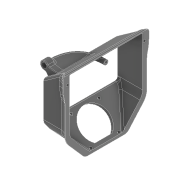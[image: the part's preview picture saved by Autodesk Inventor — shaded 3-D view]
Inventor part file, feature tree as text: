
AUTODESK INVENTOR PART (.ipt)
format: ipt  version: 2021 (Build 250183000, 183)  size: 3,283,456 bytes
history: native  units: mm
features: sketch x21, extrude x16, fillet x15, projected_geometry x11, reference x6, chamfer x5, plane x4, sweep x4, delete_face x3, other x3, hole x1, thread x1
ambient origin geometry x8: Origin, YZ Plane, XZ Plane, XY Plane, X Axis, Y Axis, Z Axis, Center Point
bodies: Volumenkörper1 (feature_tree), Body6 (feature_tree)
feature tree (90):
  extrude  "Extrusion1"  Depth=3.0mm TaperAngle=0.0deg
  extrude  "Extrusion2"  Depth=11.5mm
  fillet  "Rundung1"  Radius=4.6mm
  fillet  "Rundung3"  Radius=4.6mm
  extrude  "Extrusion3"  Depth=10.0mm
  sketch  "Skizze5"  dims[d13=1.0mm d14=4.1mm]
  plane  "Arbeitsebene1"
  sketch  "Skizze6"  dims[d15=8.1mm d16=0.0mm d17=0.0mm]
  sweep  "Sweeping1"
  extrude  "Extrusion4"  TaperAngle=0.0deg  [1 undecoded]
  sketch  "Skizze9"  dims[d28=9.7mm d29=19.456mm d30=4.0mm d31=2.0mm d32=90.0deg d33=11.0mm d34=0.0mm d35=14.0mm d36=0.0mm]
  sketch  "Skizze10"  dims[d37=14.0mm d38=0.0mm d39=45.0mm d40=0.0mm]
  hole  "Bohrung1"  [1 undecoded]
  extrude  "Extrusion5"  Depth=14.0mm TaperAngle=0.0deg
  extrude  "Extrusion6"  Depth=45.0mm TaperAngle=0.0deg
  extrude  "Extrusion7"  Depth=10.0mm TaperAngle=0.0deg
  extrude  "Extrusion8"  Depth=10.0mm TaperAngle=0.0deg
  plane  "Arbeitsebene3"
  extrude  "Extrusion9"  Depth=30.0mm TaperAngle=0.0deg
  plane  "Arbeitsebene2"
  extrude  "Extrusion10"  TaperAngle=0.0deg  [1 undecoded]
  sweep  "Sweeping2"
  extrude  "Extrusion11"  Depth=10.0mm TaperAngle=0.0deg
  extrude  "Extrusion12"  Depth=5.0mm
  sweep  "Sweeping3"
  extrude  "Extrusion13"  Depth=4.0mm
  fillet  "Rundung8"  Radius=9.599311mm
  fillet  "Rundung9"  Radius=9.599311mm
  extrude  "Extrusion14"  TaperAngle=0.0deg  [1 undecoded]
  fillet  "Rundung10"  Radius=10.0mm
  fillet  "Rundung11"  Radius=7.9mm
  fillet  "Rundung12"  Radius=7.9mm
  fillet  "Rundung13"  Radius=1.0mm
  fillet  "Rundung14"  Radius=1.604mm
  fillet  "Rundung15"  Radius=2.19mm
  plane  "Arbeitsebene4"
  sweep  "Sweeping4"
  thread  "Gewinde3"  [1 undecoded]
  chamfer  "Fase5"  Distance=19.0mm
  chamfer  "Fase6"  Distance=33.0mm
  extrude  "Extrusion15"  Depth=2.0mm
  chamfer  "Fase7"  Distance=1.0mm
  chamfer  "Fase8"  [1 undecoded]
  chamfer  "Fase9"  [1 undecoded]
  fillet  "Rundung19"  [1 undecoded]
  fillet  "Rundung20"  [1 undecoded]
  delete_face  "Fläche löschen1"
  delete_face  "Fläche löschen2"
  delete_face  "Fläche löschen3"
  fillet  "Rundung21"  [1 undecoded]
  fillet  "Rundung22"  [1 undecoded]
  fillet  "Rundung23"  [1 undecoded]
  extrude  "Extrusion16"  [1 undecoded]
  sketch  "Skizze1"  dims[d0=0.0mm d1=0.0mm d3=3.0mm d4=0.0mm]
  sketch  "Skizze2"  dims[d5=4.7mm d6=11.5mm d7=4.6mm d9=4.6mm]
  sketch  "Skizze4"  dims[d10=10.0mm d11=0.0mm d12=15.0mm]
  reference  "Referenz1"
  reference  "Referenz2"
  reference  "Referenz3"
  reference  "Referenz4"
  reference  "Referenz5"
  reference  "Referenz6"
  sketch  "Skizze8"  dims[d23=15.0mm d24=10.0mm d25=0.0mm]
  projected_geometry  "Projizierte Kontur4"
  projected_geometry  "Projizierte Kontur5"
  sketch  "Skizze11"  dims[d41=10.0mm d42=0.0mm d43=30.0mm d44=0.0mm]
  sketch  "Skizze12"  dims[d45=11.75mm d46=10.0mm d47=0.0mm]
  projected_geometry  "Projizierte Kontur6"
  sketch  "Skizze13"  dims[d48=0.0mm d49=0.0mm d50=30.0mm d51=0.0mm]
  sketch  "Skizze14"  dims[d52=10.0mm d53=0.0mm d54=0.0mm d55=0.0mm]
  projected_geometry  "Projizierte Kontur7"
  sketch  "Skizze15"  dims[d56=1.0mm d57=0.0mm d58=100.0mm]
  projected_geometry  "Projizierte Kontur8"
  sketch  "Skizze17"  dims[d59=12.0mm d60=10.0mm d61=0.0mm]
  projected_geometry  "Projizierte Kontur9"
  sketch  "Skizze18"  dims[d62=5.0mm d63=5.0mm]
  projected_geometry  "Projizierte Kontur10"
  sketch  "Skizze19"  dims[d64=5.0mm d65=3.0mm]
  projected_geometry  "Projizierte Kontur11"
  sketch  "Skizze20"  dims[d66=1.0mm d67=4.0mm d81=9.599311mm d104=9.599311mm]
  projected_geometry  "Projizierte Kontur12"
  sketch  "Skizze21"  dims[d120=4.4mm d121=0.0mm d122=0.0mm d123=10.0mm d124=0.0mm]
  projected_geometry  "Projizierte Kontur13"
  sketch  "Skizze26"  dims[d125=2.0mm d126=2.0mm d127=45.0deg]
  sketch  "Skizze27"  dims[d128=0.4mm d129=2.0mm d130=45.0deg d131=7.9mm d132=7.9mm d133=1.0mm d134=0.0mm]
  sketch  "Skizze28"  dims[d135=2.45mm d136=2.0mm d137=45.0deg d138=1.604mm d139=1.0mm d140=45.0deg d141=2.19mm d142=1.0mm d143=45.0deg d144=3.0mm d145=18.0mm d146=19.0mm d147=33.0mm d148=2.0mm d149=1.0mm d150=0.0mm]
  projected_geometry  "Projizierte Kontur14"
  other  "<userpath>\Downloads\VORON2_v2.4_Assembly_Step\Exhast Filter Housing v12.iam"
  other  "Exhast Filter Housing v12.iam"
  other  "Exhast Grill:1"
note: 13 required parameter values undecoded (feature->parameter linkage not recoverable at this tier; creation-order binding heuristic only, values carry confidence <= 0.55)
